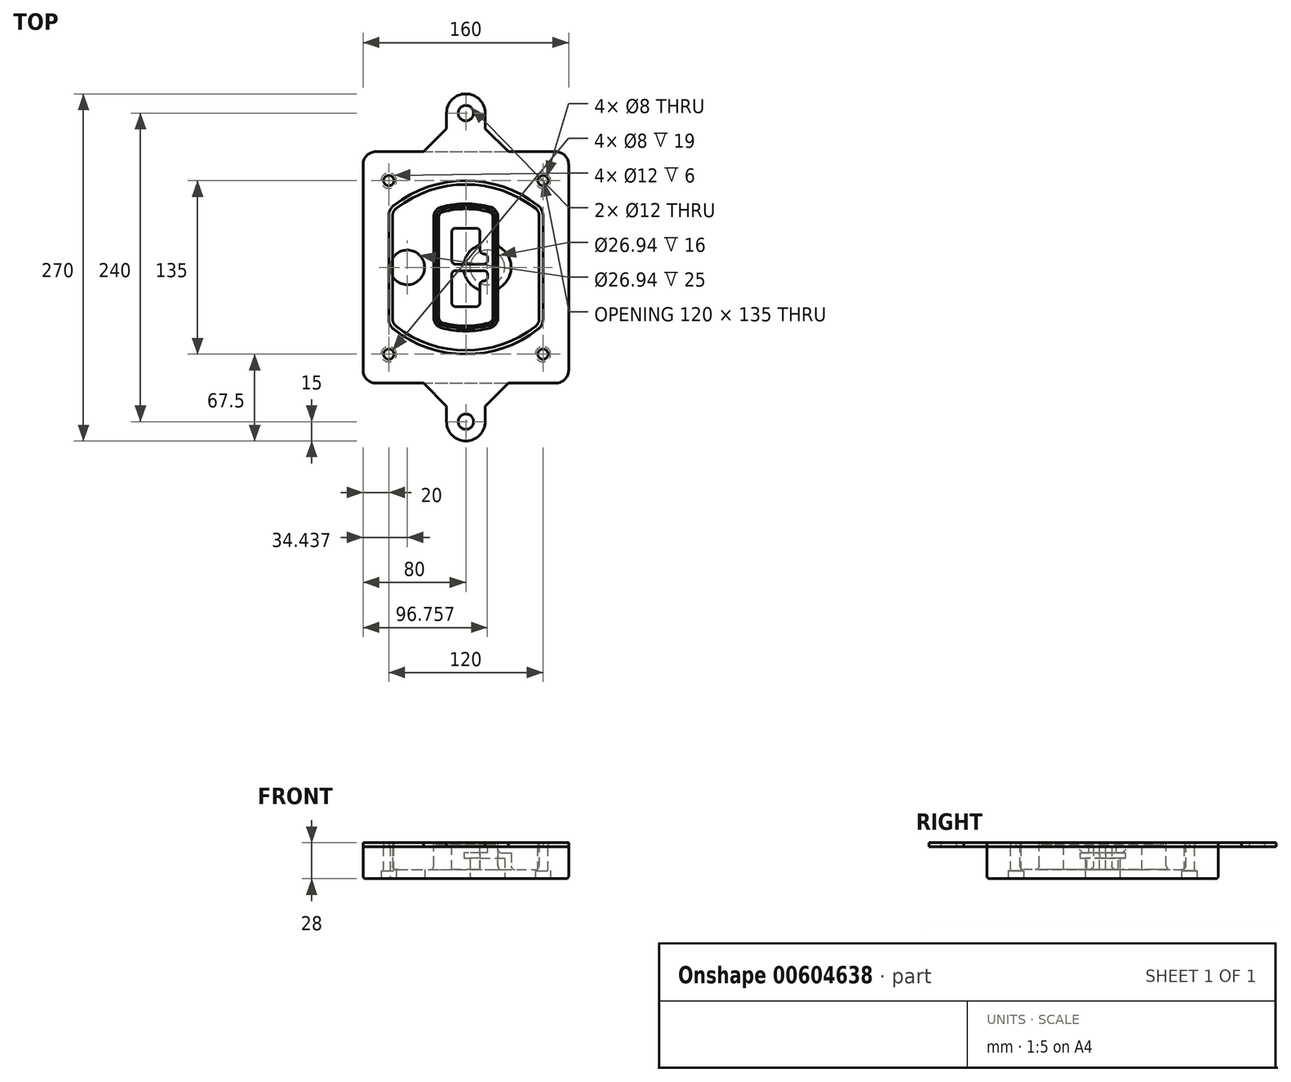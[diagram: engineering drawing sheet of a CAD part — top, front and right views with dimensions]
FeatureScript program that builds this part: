
annotation { "Feature Type Name" : "Feature", "Feature Type Description" : "" }
export const myFeature = defineFeature(function(context is Context, id is Id, definition is map)
    precondition{}
    {
        {
            var Q0;
            Q0=qCreatedBy(makeId("Top.planeOp"),FACE);
            var sketch = newSketch(context, id + "F0", { "sketchPlane" : qUnion([Q0])});
            skPoint(sketch, "E0.rect.middle", {"position": v(0, 0) * mm});
            skLineSegment(sketch, "E1.bottom", {"start": v(-70, -90) * mm, "end": v(70, -90) * mm});
            skLineSegment(sketch, "E1.top", {"start": v(-70, 90) * mm, "end": v(70, 90) * mm});
            skLineSegment(sketch, "E1.left", {"start": v(-80, -80) * mm, "end": v(-80, 80) * mm});
            skLineSegment(sketch, "E1.right", {"start": v(80, -80) * mm, "end": v(80, 80) * mm});
            skLineSegment(sketch, "E2", {"start": v(-80, 90) * mm, "end": v(80, -90) * mm, "construction": true});
            skLineSegment(sketch, "E3", {"start": v(80, 90) * mm, "end": v(-80, -90) * mm, "construction": true});
            skCircle(sketch, "E4", {"center": v(-60, 67.5) * mm, "radius": 4 * mm});
            skCircle(sketch, "E5", {"center": v(60, 67.5) * mm, "radius": 4 * mm});
            skCircle(sketch, "E6", {"center": v(60, -67.5) * mm, "radius": 4 * mm});
            skCircle(sketch, "E7", {"center": v(-60, -67.5) * mm, "radius": 4 * mm});
            skLineSegment(sketch, "E8", {"start": v(-60, 67.5) * mm, "end": v(60, 67.5) * mm, "construction": true});
            skLineSegment(sketch, "E9", {"start": v(60, 67.5) * mm, "end": v(60, -67.5) * mm, "construction": true});
            skLineSegment(sketch, "E10", {"start": v(60, -67.5) * mm, "end": v(-60, -67.5) * mm, "construction": true});
            skLineSegment(sketch, "E11", {"start": v(-60, -67.5) * mm, "end": v(-60, 67.5) * mm, "construction": true});
            skLineSegment(sketch, "E12", {"start": v(-60, 40.3) * mm, "end": v(-60, -40.3) * mm});
            skLineSegment(sketch, "E13", {"start": v(60, 40.3) * mm, "end": v(60, -40.3) * mm});
            skArc(sketch, "E14", {"start": v(56.15, 48.18) * mm, "mid": v(0, 67.5) * mm, "end": v(-56.15, 48.18) * mm});
            skArc(sketch, "E15", {"start": v(-56.15, -48.18) * mm, "mid": v(0, -67.5) * mm, "end": v(56.15, -48.18) * mm});
            skLineSegment(sketch, "E16", {"start": v(-60, 0) * mm, "end": v(60, 0) * mm, "construction": true});
            skPoint(sketch, "E17.visualSharp", {"position": v(-60, -45) * mm});
            skArc(sketch, "E17.filletArc", {"start": v(-60, -40.3) * mm, "mid": v(-58.99, -44.68) * mm, "end": v(-56.15, -48.18) * mm});
            skPoint(sketch, "E18.visualSharp", {"position": v(-60, 45) * mm});
            skArc(sketch, "E18.filletArc", {"start": v(-56.15, 48.18) * mm, "mid": v(-58.99, 44.68) * mm, "end": v(-60, 40.3) * mm});
            skPoint(sketch, "E19.visualSharp", {"position": v(60, 45) * mm});
            skArc(sketch, "E19.filletArc", {"start": v(60, 40.3) * mm, "mid": v(58.99, 44.68) * mm, "end": v(56.15, 48.18) * mm});
            skPoint(sketch, "E20.visualSharp", {"position": v(60, -45) * mm});
            skArc(sketch, "E20.filletArc", {"start": v(56.15, -48.18) * mm, "mid": v(58.99, -44.68) * mm, "end": v(60, -40.3) * mm});
            skPoint(sketch, "E21.visualSharp", {"position": v(-80, 90) * mm});
            skArc(sketch, "E21.filletArc", {"start": v(-70, 90) * mm, "mid": v(-77.07, 87.07) * mm, "end": v(-80, 80) * mm});
            skPoint(sketch, "E22.visualSharp", {"position": v(80, 90) * mm});
            skArc(sketch, "E22.filletArc", {"start": v(80, 80) * mm, "mid": v(77.07, 87.07) * mm, "end": v(70, 90) * mm});
            skPoint(sketch, "E23.visualSharp", {"position": v(80, -90) * mm});
            skArc(sketch, "E23.filletArc", {"start": v(70, -90) * mm, "mid": v(77.07, -87.07) * mm, "end": v(80, -80) * mm});
            skPoint(sketch, "E24.visualSharp", {"position": v(-80, -90) * mm});
            skArc(sketch, "E24.filletArc", {"start": v(-80, -80) * mm, "mid": v(-77.07, -87.07) * mm, "end": v(-70, -90) * mm});
            skArc(sketch, "E25.0", {"start": v(57, 40.3) * mm, "mid": v(56.3, 43.36) * mm, "end": v(54.3, 45.81) * mm});
            skLineSegment(sketch, "E25.1", {"start": v(57, 40.3) * mm, "end": v(57, -40.3) * mm});
            skArc(sketch, "E25.2", {"start": v(54.3, -45.81) * mm, "mid": v(56.3, -43.36) * mm, "end": v(57, -40.3) * mm});
            skArc(sketch, "E25.3", {"start": v(-54.3, -45.81) * mm, "mid": v(0, -64.5) * mm, "end": v(54.3, -45.81) * mm});
            skArc(sketch, "E25.4", {"start": v(-57, -40.3) * mm, "mid": v(-56.3, -43.36) * mm, "end": v(-54.3, -45.81) * mm});
            skArc(sketch, "E25.5", {"start": v(54.3, 45.81) * mm, "mid": v(0, 64.5) * mm, "end": v(-54.3, 45.81) * mm});
            skLineSegment(sketch, "E25.6", {"start": v(-57, 40.3) * mm, "end": v(-57, -40.3) * mm});
            skArc(sketch, "E25.7", {"start": v(-54.3, 45.81) * mm, "mid": v(-56.3, 43.36) * mm, "end": v(-57, 40.3) * mm});
            skArc(sketch, "E26.0", {"start": v(-58.62, 51.33) * mm, "mid": v(-62.58, 46.43) * mm, "end": v(-64, 40.3) * mm});
            skArc(sketch, "E26.1", {"start": v(58.62, 51.33) * mm, "mid": v(0, 71.5) * mm, "end": v(-58.62, 51.33) * mm});
            skArc(sketch, "E26.2", {"start": v(64, 40.3) * mm, "mid": v(62.58, 46.43) * mm, "end": v(58.62, 51.33) * mm});
            skLineSegment(sketch, "E26.3", {"start": v(64, 40.3) * mm, "end": v(64, -40.3) * mm});
            skArc(sketch, "E26.4", {"start": v(58.62, -51.33) * mm, "mid": v(62.58, -46.43) * mm, "end": v(64, -40.3) * mm});
            skLineSegment(sketch, "E26.5", {"start": v(-64, 40.3) * mm, "end": v(-64, -40.3) * mm});
            skArc(sketch, "E26.6", {"start": v(-58.62, -51.33) * mm, "mid": v(0, -71.5) * mm, "end": v(58.62, -51.33) * mm});
            skArc(sketch, "E26.7", {"start": v(-64, -40.3) * mm, "mid": v(-62.58, -46.43) * mm, "end": v(-58.62, -51.33) * mm});
            skSolve(sketch);
        }
        {
            var Q0;
            Q0=makeQuery(id+"F0.imprint","IMPRINT",FACE,{"disambiguationData":[TD([[makeQuery(id+"F0.imprint","IMPRINT",EDGE,{"derivedFrom":sQuery(id+"F0.wireOp",EDGE,"E1.bottom")}),1.0]])]});
            var Q1;
            Q1=makeQuery(id+"F0.imprint","IMPRINT",FACE,{"disambiguationData":[TD([[makeQuery(id+"F0.imprint","IMPRINT",EDGE,{"derivedFrom":sQuery(id+"F0.wireOp",EDGE,"E12")}),1.0]])]});
            var Q2;
            Q2=makeQuery(id+"F0.imprint","IMPRINT",FACE,{"disambiguationData":[TD([[makeQuery(id+"F0.imprint","IMPRINT",EDGE,{"derivedFrom":sQuery(id+"F0.wireOp",EDGE,"E25.0")}),1.0]])]});
            var Q3;
            Q3=makeQuery(id+"F0.imprint","IMPRINT",FACE,{"disambiguationData":[TD([[makeQuery(id+"F0.imprint","IMPRINT",EDGE,{"derivedFrom":sQuery(id+"F0.wireOp",EDGE,"E12")}),-1.0]])]});
            extrude(context, id + "F1", {"entities" : qUnion([Q0, Q1, Q2, Q3]), "oppositeDirection" : true, "depth" : 25 * mm});
        }
        {
            var Q0;
            Q0=makeQuery(id+"F0.imprint","IMPRINT",FACE,{"disambiguationData":[TD([[makeQuery(id+"F0.imprint","IMPRINT",EDGE,{"derivedFrom":sQuery(id+"F0.wireOp",EDGE,"E12")}),1.0]])]});
            extrude(context, id + "F2", {"entities" : qUnion([Q0]), "operationType" : NewBodyOperationType.ADD, "depth" : 3 * mm});
        }
        {
            var Q0;
            Q0=makeQuery(id+"F0.imprint","IMPRINT",FACE,{"disambiguationData":[TD([[makeQuery(id+"F0.imprint","IMPRINT",EDGE,{"derivedFrom":sQuery(id+"F0.wireOp",EDGE,"E25.0")}),1.0]])]});
            extrude(context, id + "F3", {"entities" : qUnion([Q0]), "operationType" : NewBodyOperationType.REMOVE, "oppositeDirection" : true, "depth" : 18 * mm});
        }
        {
            var Q0;
            Q0=makeQuery(id+"F2.opExtrude","CAP_FACE",FACE,{"disambiguationData":[OSD([sQuery(id+"F0.wireOp",EDGE,"E12"),sQuery(id+"F0.wireOp",EDGE,"E13"),sQuery(id+"F0.wireOp",EDGE,"E14"),sQuery(id+"F0.wireOp",EDGE,"E15"),sQuery(id+"F0.wireOp",EDGE,"E17.filletArc"),sQuery(id+"F0.wireOp",EDGE,"E18.filletArc"),sQuery(id+"F0.wireOp",EDGE,"E19.filletArc"),sQuery(id+"F0.wireOp",EDGE,"E20.filletArc"),sQuery(id+"F0.wireOp",EDGE,"E25.0"),sQuery(id+"F0.wireOp",EDGE,"E25.1"),sQuery(id+"F0.wireOp",EDGE,"E25.2"),sQuery(id+"F0.wireOp",EDGE,"E25.3"),sQuery(id+"F0.wireOp",EDGE,"E25.4"),sQuery(id+"F0.wireOp",EDGE,"E25.5"),sQuery(id+"F0.wireOp",EDGE,"E25.6"),sQuery(id+"F0.wireOp",EDGE,"E25.7")])],"isStart":false});
            var sketch = newSketch(context, id + "F4", { "sketchPlane" : qUnion([Q0])});
            skArc(sketch, "E27.0", {"start": v(-19.08, -46.97) * mm, "mid": v(0, -49.5) * mm, "end": v(19.08, -46.97) * mm});
            skArc(sketch, "E28.0", {"start": v(19.08, 46.97) * mm, "mid": v(0, 49.5) * mm, "end": v(-19.08, 46.97) * mm});
            skLineSegment(sketch, "E29", {"start": v(-25, 39.25) * mm, "end": v(-25, -39.25) * mm});
            skLineSegment(sketch, "E30", {"start": v(25, 39.25) * mm, "end": v(25, -39.25) * mm});
            skLineSegment(sketch, "E31", {"start": v(-25, 45.1) * mm, "end": v(25, 45.1) * mm, "construction": true});
            skLineSegment(sketch, "E32", {"start": v(-25, -45.1) * mm, "end": v(25, -45.1) * mm, "construction": true});
            skPoint(sketch, "E33.visualSharp", {"position": v(-25, 45.1) * mm});
            skArc(sketch, "E33.filletArc", {"start": v(-19.08, 46.97) * mm, "mid": v(-23.35, 44.11) * mm, "end": v(-25, 39.25) * mm});
            skPoint(sketch, "E34.visualSharp", {"position": v(25, 45.1) * mm});
            skArc(sketch, "E34.filletArc", {"start": v(25, 39.25) * mm, "mid": v(23.35, 44.11) * mm, "end": v(19.08, 46.97) * mm});
            skPoint(sketch, "E35.visualSharp", {"position": v(25, -45.1) * mm});
            skArc(sketch, "E35.filletArc", {"start": v(19.08, -46.97) * mm, "mid": v(23.35, -44.11) * mm, "end": v(25, -39.25) * mm});
            skPoint(sketch, "E36.visualSharp", {"position": v(-25, -45.1) * mm});
            skArc(sketch, "E36.filletArc", {"start": v(-25, -39.25) * mm, "mid": v(-23.35, -44.11) * mm, "end": v(-19.08, -46.97) * mm});
            skArc(sketch, "E37.0", {"start": v(54.3, 45.81) * mm, "mid": v(0, 64.5) * mm, "end": v(-54.3, 45.81) * mm});
            skArc(sketch, "E37.1", {"start": v(-54.3, 45.81) * mm, "mid": v(-56.3, 43.36) * mm, "end": v(-57, 40.3) * mm});
            skLineSegment(sketch, "E37.2", {"start": v(-57, 40.3) * mm, "end": v(-57, -40.3) * mm});
            skArc(sketch, "E37.3", {"start": v(-57, -40.3) * mm, "mid": v(-56.3, -43.36) * mm, "end": v(-54.3, -45.81) * mm});
            skArc(sketch, "E37.4", {"start": v(-54.3, -45.81) * mm, "mid": v(0, -64.5) * mm, "end": v(54.3, -45.81) * mm});
            skArc(sketch, "E37.5", {"start": v(54.3, -45.81) * mm, "mid": v(56.3, -43.36) * mm, "end": v(57, -40.3) * mm});
            skLineSegment(sketch, "E37.6", {"start": v(57, 40.3) * mm, "end": v(57, -40.3) * mm});
            skArc(sketch, "E37.7", {"start": v(57, 40.3) * mm, "mid": v(56.3, 43.36) * mm, "end": v(54.3, 45.81) * mm});
            skLineSegment(sketch, "E38.0", {"start": v(23, 39.25) * mm, "end": v(23, -39.25) * mm});
            skArc(sketch, "E38.1", {"start": v(18.56, -45.04) * mm, "mid": v(21.76, -42.9) * mm, "end": v(23, -39.25) * mm});
            skArc(sketch, "E38.2", {"start": v(-18.56, -45.04) * mm, "mid": v(0, -47.5) * mm, "end": v(18.56, -45.04) * mm});
            skArc(sketch, "E38.3", {"start": v(-23, -39.25) * mm, "mid": v(-21.76, -42.9) * mm, "end": v(-18.56, -45.04) * mm});
            skLineSegment(sketch, "E38.4", {"start": v(-23, 39.25) * mm, "end": v(-23, -39.25) * mm});
            skArc(sketch, "E38.5", {"start": v(23, 39.25) * mm, "mid": v(21.76, 42.9) * mm, "end": v(18.56, 45.04) * mm});
            skArc(sketch, "E38.6", {"start": v(-18.56, 45.04) * mm, "mid": v(-21.76, 42.9) * mm, "end": v(-23, 39.25) * mm});
            skArc(sketch, "E38.7", {"start": v(18.56, 45.04) * mm, "mid": v(0, 47.5) * mm, "end": v(-18.56, 45.04) * mm});
            skArc(sketch, "E39.0", {"start": v(21, 39.25) * mm, "mid": v(20.18, 41.68) * mm, "end": v(18.04, 43.1) * mm});
            skLineSegment(sketch, "E39.1", {"start": v(21, 39.25) * mm, "end": v(21, -39.25) * mm});
            skArc(sketch, "E39.2", {"start": v(18.04, -43.1) * mm, "mid": v(20.18, -41.68) * mm, "end": v(21, -39.25) * mm});
            skArc(sketch, "E39.3", {"start": v(-18.04, -43.1) * mm, "mid": v(0, -45.5) * mm, "end": v(18.04, -43.1) * mm});
            skArc(sketch, "E39.4", {"start": v(-21, -39.25) * mm, "mid": v(-20.18, -41.68) * mm, "end": v(-18.04, -43.1) * mm});
            skArc(sketch, "E39.5", {"start": v(18.04, 43.1) * mm, "mid": v(0, 45.5) * mm, "end": v(-18.04, 43.1) * mm});
            skLineSegment(sketch, "E39.6", {"start": v(-21, 39.25) * mm, "end": v(-21, -39.25) * mm});
            skArc(sketch, "E39.7", {"start": v(-18.04, 43.1) * mm, "mid": v(-20.18, 41.68) * mm, "end": v(-21, 39.25) * mm});
            skLineSegment(sketch, "E40", {"start": v(-25, 0) * mm, "end": v(25, 0) * mm, "construction": true});
            skLineSegment(sketch, "E41", {"start": v(-11, 5.5) * mm, "end": v(-11, 27.5) * mm});
            skLineSegment(sketch, "E42", {"start": v(-8, 30.5) * mm, "end": v(8, 30.5) * mm});
            skLineSegment(sketch, "E43", {"start": v(11, 27.5) * mm, "end": v(11, 13.5) * mm});
            skLineSegment(sketch, "E44", {"start": v(14, 10.5) * mm, "end": v(14, 10.5) * mm});
            skLineSegment(sketch, "E45", {"start": v(17, 7.5) * mm, "end": v(17, 5.5) * mm});
            skLineSegment(sketch, "E46", {"start": v(14, 2.5) * mm, "end": v(-8, 2.5) * mm});
            skPoint(sketch, "E47.visualSharp", {"position": v(-11, 30.5) * mm});
            skArc(sketch, "E47.filletArc", {"start": v(-8, 30.5) * mm, "mid": v(-10.12, 29.62) * mm, "end": v(-11, 27.5) * mm});
            skPoint(sketch, "E48.visualSharp", {"position": v(11, 30.5) * mm});
            skArc(sketch, "E48.filletArc", {"start": v(11, 27.5) * mm, "mid": v(10.12, 29.62) * mm, "end": v(8, 30.5) * mm});
            skPoint(sketch, "E49.visualSharp", {"position": v(11, 10.5) * mm});
            skArc(sketch, "E49.filletArc", {"start": v(11, 13.5) * mm, "mid": v(11.88, 11.38) * mm, "end": v(14, 10.5) * mm});
            skPoint(sketch, "E50.visualSharp", {"position": v(17, 10.5) * mm});
            skArc(sketch, "E50.filletArc", {"start": v(17, 7.5) * mm, "mid": v(16.12, 9.62) * mm, "end": v(14, 10.5) * mm});
            skPoint(sketch, "E51.visualSharp", {"position": v(17, 2.5) * mm});
            skArc(sketch, "E51.filletArc", {"start": v(14, 2.5) * mm, "mid": v(16.12, 3.38) * mm, "end": v(17, 5.5) * mm});
            skPoint(sketch, "E52.visualSharp", {"position": v(-11, 2.5) * mm});
            skArc(sketch, "E52.filletArc", {"start": v(-11, 5.5) * mm, "mid": v(-10.12, 3.38) * mm, "end": v(-8, 2.5) * mm});
            skLineSegment(sketch, "E53.0.MirrorCS", {"start": v(14, -2.5) * mm, "end": v(-8, -2.5) * mm});
            skArc(sketch, "E54.0.MirrorCS", {"start": v(-11, -5.5) * mm, "mid": v(-10.12, -3.38) * mm, "end": v(-8, -2.5) * mm});
            skLineSegment(sketch, "E55.0.MirrorCS", {"start": v(-11, -5.5) * mm, "end": v(-11, -27.5) * mm});
            skArc(sketch, "E56.0.MirrorCS", {"start": v(-8, -30.5) * mm, "mid": v(-10.12, -29.62) * mm, "end": v(-11, -27.5) * mm});
            skLineSegment(sketch, "E57.0.MirrorCS", {"start": v(-8, -30.5) * mm, "end": v(8, -30.5) * mm});
            skArc(sketch, "E58.0.MirrorCS", {"start": v(11, -27.5) * mm, "mid": v(10.12, -29.62) * mm, "end": v(8, -30.5) * mm});
            skLineSegment(sketch, "E59.0.MirrorCS", {"start": v(11, -27.5) * mm, "end": v(11, -13.5) * mm});
            skArc(sketch, "E60.0.MirrorCS", {"start": v(11, -13.5) * mm, "mid": v(11.88, -11.38) * mm, "end": v(14, -10.5) * mm});
            skArc(sketch, "E61.0.MirrorCS", {"start": v(17, -7.5) * mm, "mid": v(16.12, -9.62) * mm, "end": v(14, -10.5) * mm});
            skLineSegment(sketch, "E62.0.MirrorCS", {"start": v(17, -7.5) * mm, "end": v(17, -5.5) * mm});
            skArc(sketch, "E63.0.MirrorCS", {"start": v(14, -2.5) * mm, "mid": v(16.12, -3.38) * mm, "end": v(17, -5.5) * mm});
            skSolve(sketch);
        }
        {
            var Q0;
            Q0=makeQuery(id+"F4.imprint","IMPRINT",FACE,{"disambiguationData":[TD([[makeQuery(id+"F4.imprint","IMPRINT",EDGE,{"derivedFrom":sQuery(id+"F4.wireOp",EDGE,"E27.0")}),1.0]])]});
            var Q1;
            Q1=makeQuery(id+"F4.imprint","IMPRINT",FACE,{"disambiguationData":[TD([[makeQuery(id+"F4.imprint","IMPRINT",EDGE,{"derivedFrom":sQuery(id+"F4.wireOp",EDGE,"E38.0")}),-1.0]])]});
            var Q2;
            Q2=makeQuery(id+"F4.imprint","IMPRINT",FACE,{"disambiguationData":[TD([[makeQuery(id+"F4.imprint","IMPRINT",EDGE,{"derivedFrom":sQuery(id+"F4.wireOp",EDGE,"E39.0")}),1.0]])]});
            extrude(context, id + "F5", {"entities" : qUnion([Q0, Q1, Q2]), "operationType" : NewBodyOperationType.ADD, "endBound" : BoundingType.UP_TO_NEXT, "oppositeDirection" : true, "depth" : 25 * mm});
        }
        {
            var Q0;
            Q0=makeQuery(id+"F4.imprint","IMPRINT",FACE,{"disambiguationData":[TD([[makeQuery(id+"F4.imprint","IMPRINT",EDGE,{"derivedFrom":sQuery(id+"F4.wireOp",EDGE,"E38.0")}),-1.0]])]});
            extrude(context, id + "F6", {"entities" : qUnion([Q0]), "operationType" : NewBodyOperationType.REMOVE, "oppositeDirection" : true, "depth" : 2 * mm});
        }
        {
            var Q0;
            Q0=makeQuery(id+"F1.opExtrude","CAP_FACE",FACE,{"disambiguationData":[OSD([sQuery(id+"F0.wireOp",EDGE,"E1.bottom"),sQuery(id+"F0.wireOp",EDGE,"E1.top"),sQuery(id+"F0.wireOp",EDGE,"E1.left"),sQuery(id+"F0.wireOp",EDGE,"E1.right"),sQuery(id+"F0.wireOp",EDGE,"E4"),sQuery(id+"F0.wireOp",EDGE,"E5"),sQuery(id+"F0.wireOp",EDGE,"E6"),sQuery(id+"F0.wireOp",EDGE,"E7"),sQuery(id+"F0.wireOp",EDGE,"E21.filletArc"),sQuery(id+"F0.wireOp",EDGE,"E22.filletArc"),sQuery(id+"F0.wireOp",EDGE,"E23.filletArc"),sQuery(id+"F0.wireOp",EDGE,"E24.filletArc")])],"isStart":false});
            var sketch = newSketch(context, id + "F7", { "sketchPlane" : qUnion([Q0])});
            skCircle(sketch, "E64", {"center": v(16.76, 0) * mm, "radius": 13.47 * mm});
            skCircle(sketch, "E65", {"center": v(-45.56, 0) * mm, "radius": 13.47 * mm});
            skLineSegment(sketch, "E66", {"start": v(80, 0) * mm, "end": v(-80, 0) * mm});
            skCircle(sketch, "E67", {"center": v(16.76, 0) * mm, "radius": 18.47 * mm});
            skCircle(sketch, "E68", {"center": v(60, -67.5) * mm, "radius": 6 * mm});
            skCircle(sketch, "E69", {"center": v(-60, -67.5) * mm, "radius": 6 * mm});
            skCircle(sketch, "E70", {"center": v(-60, 67.5) * mm, "radius": 6 * mm});
            skCircle(sketch, "E71", {"center": v(60, 67.5) * mm, "radius": 6 * mm});
            skSolve(sketch);
        }
        {
            var Q0;
            {var subQ1=sQuery(id+"F7.wireOp",EDGE,"E66");var subQ4=sQuery(id+"F7.wireOp",EDGE,"E64");var subQ6=makeQuery(id+"F7.imprint","INTERSECT",VERTEX,{"disambiguationData":[OD(0.0)],"derivedFrom":[subQ4,subQ1]});Q0=makeQuery(id+"F7.imprint","IMPRINT",FACE,{"disambiguationData":[TD([[makeQuery(id+"F7.imprint","IMPRINT",EDGE,{"disambiguationData":[TD([[subQ6,-1.0]])],"derivedFrom":subQ4}),-1.0]])]});}
            var Q1;
            {var subQ0=sQuery(id+"F7.wireOp",EDGE,"E66");var subQ1=sQuery(id+"F7.wireOp",EDGE,"E64");var subQ3=makeQuery(id+"F7.imprint","INTERSECT",VERTEX,{"disambiguationData":[OD(0.0)],"derivedFrom":[subQ1,subQ0]});Q1=makeQuery(id+"F7.imprint","IMPRINT",FACE,{"disambiguationData":[TD([[makeQuery(id+"F7.imprint","IMPRINT",EDGE,{"disambiguationData":[TD([[subQ3,-1.0]])],"derivedFrom":subQ1}),1.0]])]});}
            var Q2;
            {var subQ0=sQuery(id+"F7.wireOp",EDGE,"E66");var subQ1=sQuery(id+"F7.wireOp",EDGE,"E64");var subQ3=makeQuery(id+"F7.imprint","INTERSECT",VERTEX,{"disambiguationData":[OD(0.0)],"derivedFrom":[subQ1,subQ0]});Q2=makeQuery(id+"F7.imprint","IMPRINT",FACE,{"disambiguationData":[TD([[makeQuery(id+"F7.imprint","IMPRINT",EDGE,{"disambiguationData":[TD([[subQ3,1.0]])],"derivedFrom":subQ1}),1.0]])]});}
            var Q3;
            {var subQ1=sQuery(id+"F7.wireOp",EDGE,"E66");var subQ4=sQuery(id+"F7.wireOp",EDGE,"E64");var subQ6=makeQuery(id+"F7.imprint","INTERSECT",VERTEX,{"disambiguationData":[OD(0.0)],"derivedFrom":[subQ4,subQ1]});Q3=makeQuery(id+"F7.imprint","IMPRINT",FACE,{"disambiguationData":[TD([[makeQuery(id+"F7.imprint","IMPRINT",EDGE,{"disambiguationData":[TD([[subQ6,1.0]])],"derivedFrom":subQ4}),-1.0]])]});}
            extrude(context, id + "F8", {"entities" : qUnion([Q0, Q1, Q2, Q3]), "operationType" : NewBodyOperationType.ADD, "oppositeDirection" : true, "depth" : 20 * mm});
        }
        {
            var Q0;
            {var subQ0=sQuery(id+"F7.wireOp",EDGE,"E66");var subQ1=sQuery(id+"F7.wireOp",EDGE,"E64");var subQ3=makeQuery(id+"F7.imprint","INTERSECT",VERTEX,{"disambiguationData":[OD(0.0)],"derivedFrom":[subQ1,subQ0]});Q0=makeQuery(id+"F7.imprint","IMPRINT",FACE,{"disambiguationData":[TD([[makeQuery(id+"F7.imprint","IMPRINT",EDGE,{"disambiguationData":[TD([[subQ3,-1.0]])],"derivedFrom":subQ1}),1.0]])]});}
            var Q1;
            {var subQ0=sQuery(id+"F7.wireOp",EDGE,"E66");var subQ1=sQuery(id+"F7.wireOp",EDGE,"E64");var subQ3=makeQuery(id+"F7.imprint","INTERSECT",VERTEX,{"disambiguationData":[OD(0.0)],"derivedFrom":[subQ1,subQ0]});Q1=makeQuery(id+"F7.imprint","IMPRINT",FACE,{"disambiguationData":[TD([[makeQuery(id+"F7.imprint","IMPRINT",EDGE,{"disambiguationData":[TD([[subQ3,1.0]])],"derivedFrom":subQ1}),1.0]])]});}
            extrude(context, id + "F9", {"entities" : qUnion([Q0, Q1]), "operationType" : NewBodyOperationType.REMOVE, "oppositeDirection" : true, "depth" : 16 * mm});
        }
        {
            var Q0;
            {var subQ0=sQuery(id+"F7.wireOp",EDGE,"E66");var subQ1=sQuery(id+"F7.wireOp",EDGE,"E65");var subQ3=makeQuery(id+"F7.imprint","INTERSECT",VERTEX,{"disambiguationData":[OD(0.0)],"derivedFrom":[subQ1,subQ0]});Q0=makeQuery(id+"F7.imprint","IMPRINT",FACE,{"disambiguationData":[TD([[makeQuery(id+"F7.imprint","IMPRINT",EDGE,{"disambiguationData":[TD([[subQ3,-1.0]])],"derivedFrom":subQ1}),1.0]])]});}
            var Q1;
            {var subQ0=sQuery(id+"F7.wireOp",EDGE,"E66");var subQ1=sQuery(id+"F7.wireOp",EDGE,"E65");var subQ3=makeQuery(id+"F7.imprint","INTERSECT",VERTEX,{"disambiguationData":[OD(0.0)],"derivedFrom":[subQ1,subQ0]});Q1=makeQuery(id+"F7.imprint","IMPRINT",FACE,{"disambiguationData":[TD([[makeQuery(id+"F7.imprint","IMPRINT",EDGE,{"disambiguationData":[TD([[subQ3,1.0]])],"derivedFrom":subQ1}),1.0]])]});}
            extrude(context, id + "F10", {"entities" : qUnion([Q0, Q1]), "operationType" : NewBodyOperationType.REMOVE, "oppositeDirection" : true, "depth" : 25 * mm});
        }
        {
            var Q0;
            Q0=makeQuery(id+"F7.imprint","IMPRINT",FACE,{"disambiguationData":[TD([[makeQuery(id+"F7.imprint","IMPRINT",EDGE,{"derivedFrom":sQuery(id+"F7.wireOp",EDGE,"E68")}),1.0]])]});
            var Q1;
            Q1=makeQuery(id+"F7.imprint","IMPRINT",FACE,{"disambiguationData":[TD([[makeQuery(id+"F7.imprint","IMPRINT",EDGE,{"derivedFrom":makeQuery(id+"F1.opExtrude","CAP_EDGE",EDGE,{"disambiguationData":[OSD([sQuery(id+"F0.wireOp",EDGE,"E5")])],"isStart":false})}),-1.0]])]});
            var Q2;
            Q2=makeQuery(id+"F7.imprint","IMPRINT",FACE,{"disambiguationData":[TD([[makeQuery(id+"F7.imprint","IMPRINT",EDGE,{"derivedFrom":sQuery(id+"F7.wireOp",EDGE,"E69")}),1.0]])]});
            var Q3;
            Q3=makeQuery(id+"F7.imprint","IMPRINT",FACE,{"disambiguationData":[TD([[makeQuery(id+"F7.imprint","IMPRINT",EDGE,{"derivedFrom":makeQuery(id+"F1.opExtrude","CAP_EDGE",EDGE,{"disambiguationData":[OSD([sQuery(id+"F0.wireOp",EDGE,"E4")])],"isStart":false})}),-1.0]])]});
            var Q4;
            Q4=makeQuery(id+"F7.imprint","IMPRINT",FACE,{"disambiguationData":[TD([[makeQuery(id+"F7.imprint","IMPRINT",EDGE,{"derivedFrom":sQuery(id+"F7.wireOp",EDGE,"E70")}),1.0]])]});
            var Q5;
            Q5=makeQuery(id+"F7.imprint","IMPRINT",FACE,{"disambiguationData":[TD([[makeQuery(id+"F7.imprint","IMPRINT",EDGE,{"derivedFrom":makeQuery(id+"F1.opExtrude","CAP_EDGE",EDGE,{"disambiguationData":[OSD([sQuery(id+"F0.wireOp",EDGE,"E7")])],"isStart":false})}),-1.0]])]});
            var Q6;
            Q6=makeQuery(id+"F7.imprint","IMPRINT",FACE,{"disambiguationData":[TD([[makeQuery(id+"F7.imprint","IMPRINT",EDGE,{"derivedFrom":sQuery(id+"F7.wireOp",EDGE,"E71")}),1.0]])]});
            var Q7;
            Q7=makeQuery(id+"F7.imprint","IMPRINT",FACE,{"disambiguationData":[TD([[makeQuery(id+"F7.imprint","IMPRINT",EDGE,{"derivedFrom":makeQuery(id+"F1.opExtrude","CAP_EDGE",EDGE,{"disambiguationData":[OSD([sQuery(id+"F0.wireOp",EDGE,"E6")])],"isStart":false})}),-1.0]])]});
            extrude(context, id + "F11", {"entities" : qUnion([Q0, Q1, Q2, Q3, Q4, Q5, Q6, Q7]), "operationType" : NewBodyOperationType.REMOVE, "oppositeDirection" : true, "depth" : 6 * mm});
        }
        {
            var Q0;
            Q0=makeQuery(id+"F9.boolean.opBoolean","COPY",FACE,{"derivedFrom":makeQuery(id+"F9.opExtrude","CAP_FACE",FACE,{"disambiguationData":[OSD([sQuery(id+"F7.wireOp",EDGE,"E64")])],"isStart":false})});
            var sketch = newSketch(context, id + "F12", { "sketchPlane" : qUnion([Q0])});
            skArc(sketch, "E72.0", {"start": v(11, 17.55) * mm, "mid": v(2.57, 11.82) * mm, "end": v(-1.54, 2.5) * mm});
            skArc(sketch, "E72.1", {"start": v(-1.54, -2.5) * mm, "mid": v(2.57, -11.82) * mm, "end": v(11, -17.55) * mm});
            skLineSegment(sketch, "E73", {"start": v(-1.54, -2.5) * mm, "end": v(14, -2.5) * mm});
            skLineSegment(sketch, "E74.0", {"start": v(14, 2.5) * mm, "end": v(-1.54, 2.5) * mm});
            skArc(sketch, "E74.1", {"start": v(14, 2.5) * mm, "mid": v(16.12, 3.38) * mm, "end": v(17, 5.5) * mm});
            skLineSegment(sketch, "E74.2", {"start": v(17, 7.5) * mm, "end": v(17, 5.5) * mm});
            skArc(sketch, "E74.3", {"start": v(17, 7.5) * mm, "mid": v(16.12, 9.62) * mm, "end": v(14, 10.5) * mm});
            skArc(sketch, "E74.4", {"start": v(11, 13.5) * mm, "mid": v(11.88, 11.38) * mm, "end": v(14, 10.5) * mm});
            skLineSegment(sketch, "E74.5", {"start": v(11, 17.55) * mm, "end": v(11, 13.5) * mm});
            skLineSegment(sketch, "E74.7", {"start": v(14, -2.5) * mm, "end": v(-1.54, -2.5) * mm});
            skArc(sketch, "E74.8", {"start": v(14, -2.5) * mm, "mid": v(16.12, -3.38) * mm, "end": v(17, -5.5) * mm});
            skLineSegment(sketch, "E74.9", {"start": v(17, -7.5) * mm, "end": v(17, -5.5) * mm});
            skArc(sketch, "E74.10", {"start": v(17, -7.5) * mm, "mid": v(16.12, -9.62) * mm, "end": v(14, -10.5) * mm});
            skArc(sketch, "E74.11", {"start": v(11, -13.5) * mm, "mid": v(11.88, -11.38) * mm, "end": v(14, -10.5) * mm});
            skLineSegment(sketch, "E74.12", {"start": v(11, -17.55) * mm, "end": v(11, -13.5) * mm});
            skPoint(sketch, "E75.orphan", {"position": v(11, -27.5) * mm});
            skPoint(sketch, "E76.orphan", {"position": v(-8, -2.5) * mm});
            skPoint(sketch, "E77.orphan", {"position": v(-8, 2.5) * mm});
            skPoint(sketch, "E78.orphan", {"position": v(11, 27.5) * mm});
            skSolve(sketch);
        }
        {
            var Q0;
            {var subQ7=sQuery(id+"F12.wireOp",EDGE,"E72.0");var subQ14=sQuery(id+"F12.wireOp",EDGE,"E72.1");var subQ16=sQuery(id+"F12.wireOp",EDGE,"E74.1");var subQ18=sQuery(id+"F12.wireOp",EDGE,"E74.8");Q0=qUnion([makeQuery(id+"F12.imprint","IMPRINT",FACE,{"disambiguationData":[TD([[makeQuery(id+"F12.imprint","IMPRINT",EDGE,{"derivedFrom":subQ7}),1.0]])]}),makeQuery(id+"F12.imprint","IMPRINT",FACE,{"disambiguationData":[TD([[makeQuery(id+"F12.imprint","IMPRINT",EDGE,{"derivedFrom":subQ14}),1.0]])]}),makeQuery(id+"F12.imprint","IMPRINT",FACE,{"disambiguationData":[TD([[makeQuery(id+"F12.imprint","IMPRINT",EDGE,{"derivedFrom":subQ16}),1.0]])]}),makeQuery(id+"F12.imprint","IMPRINT",FACE,{"disambiguationData":[TD([[makeQuery(id+"F12.imprint","IMPRINT",EDGE,{"derivedFrom":subQ18}),-1.0]])]})]);}
            var Q1;
            Q1=makeQuery(id+"F5.boolean.opBoolean","SPLIT",FACE,{"disambiguationData":[TD([makeQuery(id+"F5.opExtrude","SWEPT_FACE",FACE,{"disambiguationData":[OSD([sQuery(id+"F4.wireOp",EDGE,"E41")])]})])],"derivedFrom":makeQuery(id+"F3.boolean.opBoolean","COPY",FACE,{"derivedFrom":makeQuery(id+"F3.opExtrude","CAP_FACE",FACE,{"disambiguationData":[OSD([sQuery(id+"F0.wireOp",EDGE,"E25.0"),sQuery(id+"F0.wireOp",EDGE,"E25.1"),sQuery(id+"F0.wireOp",EDGE,"E25.2"),sQuery(id+"F0.wireOp",EDGE,"E25.3"),sQuery(id+"F0.wireOp",EDGE,"E25.4"),sQuery(id+"F0.wireOp",EDGE,"E25.5"),sQuery(id+"F0.wireOp",EDGE,"E25.6"),sQuery(id+"F0.wireOp",EDGE,"E25.7")])],"isStart":false})})});
            extrude(context, id + "F13", {"entities" : qUnion([Q0]), "operationType" : NewBodyOperationType.REMOVE, "endBound" : BoundingType.UP_TO_SURFACE, "endBoundEntityFace" : qUnion([Q1]), "depth" : 25 * mm});
        }
        {
            var Q0;
            Q0=makeQuery(id+"F3.boolean.opBoolean","COPY",EDGE,{"derivedFrom":makeQuery(id+"F3.opExtrude","CAP_EDGE",EDGE,{"disambiguationData":[OSD([sQuery(id+"F0.wireOp",EDGE,"E25.6")])],"isStart":false})});
            var Q1;
            Q1=makeQuery(id+"F8.boolean.opBoolean","INTERSECT",EDGE,{"derivedFrom":[makeQuery(id+"F5.opExtrude","SWEPT_FACE",FACE,{"disambiguationData":[OSD([sQuery(id+"F4.wireOp",EDGE,"E30")])]}),makeQuery(id+"F8.opExtrude","CAP_FACE",FACE,{"disambiguationData":[OSD([sQuery(id+"F7.wireOp",EDGE,"E67")])],"isStart":false})]});
            var Q2;
            Q2=makeQuery(id+"F8.boolean.opBoolean","INTERSECT",EDGE,{"disambiguationData":[OD(1.0)],"derivedFrom":[makeQuery(id+"F5.opExtrude","SWEPT_FACE",FACE,{"disambiguationData":[OSD([sQuery(id+"F4.wireOp",EDGE,"E30")])]}),makeQuery(id+"F8.opExtrude","SWEPT_FACE",FACE,{"disambiguationData":[OSD([sQuery(id+"F7.wireOp",EDGE,"E67")])]})]});
            var Q3;
            {var subQ0=sQuery(id+"F4.wireOp",EDGE,"E30");Q3=makeQuery(id+"F8.boolean.opBoolean","SPLIT",EDGE,{"disambiguationData":[TD([makeQuery(id+"F5.opExtrude","SWEPT_FACE",FACE,{"disambiguationData":[OSD([sQuery(id+"F4.wireOp",EDGE,"E35.filletArc")])]})])],"derivedFrom":makeQuery(id+"F5.opExtrude","CAP_EDGE",EDGE,{"disambiguationData":[OSD([subQ0])],"isStart":false})});}
            var Q4;
            {var subQ0=sQuery(id+"F0.wireOp",EDGE,"E25.7");var subQ1=sQuery(id+"F0.wireOp",EDGE,"E25.1");var subQ2=sQuery(id+"F0.wireOp",EDGE,"E25.6");var subQ3=sQuery(id+"F0.wireOp",EDGE,"E25.5");var subQ4=sQuery(id+"F0.wireOp",EDGE,"E25.4");var subQ5=sQuery(id+"F0.wireOp",EDGE,"E25.0");var subQ6=sQuery(id+"F0.wireOp",EDGE,"E25.2");var subQ7=sQuery(id+"F0.wireOp",EDGE,"E25.3");Q4=makeQuery(id+"F8.boolean.opBoolean","INTERSECT",EDGE,{"derivedFrom":[makeQuery(id+"F5.boolean.opBoolean","SPLIT",FACE,{"disambiguationData":[TD([makeQuery(id+"F2.opExtrude","SWEPT_FACE",FACE,{"disambiguationData":[OSD([subQ5])]})])],"derivedFrom":makeQuery(id+"F3.boolean.opBoolean","COPY",FACE,{"derivedFrom":makeQuery(id+"F3.opExtrude","CAP_FACE",FACE,{"disambiguationData":[OSD([subQ5,subQ1,subQ6,subQ7,subQ4,subQ3,subQ2,subQ0])],"isStart":false})})}),makeQuery(id+"F8.opExtrude","SWEPT_FACE",FACE,{"disambiguationData":[OSD([sQuery(id+"F7.wireOp",EDGE,"E67")])]})]});}
            var Q5;
            Q5=makeQuery(id+"F8.boolean.opBoolean","INTERSECT",EDGE,{"disambiguationData":[OD(0.0)],"derivedFrom":[makeQuery(id+"F5.opExtrude","SWEPT_FACE",FACE,{"disambiguationData":[OSD([sQuery(id+"F4.wireOp",EDGE,"E30")])]}),makeQuery(id+"F8.opExtrude","SWEPT_FACE",FACE,{"disambiguationData":[OSD([sQuery(id+"F7.wireOp",EDGE,"E67")])]})]});
            fillet(context, id + "F14", {"entities" : qUnion([Q0, Q1, Q2, Q3, Q4, Q5]), "radius" : 3 * mm, "tangentPropagation" : true, "allowEdgeOverflow" : false});
        }
        {
            var Q0;
            Q0=makeQuery(id+"F1.opExtrude","CAP_EDGE",EDGE,{"disambiguationData":[OSD([sQuery(id+"F0.wireOp",EDGE,"E1.bottom")])],"isStart":false});
            fillet(context, id + "F15", {"entities" : qUnion([Q0]), "radius" : 2 * mm, "tangentPropagation" : true, "allowEdgeOverflow" : false});
        }
        {
            var Q0;
            {var subQ0=sQuery(id+"F0.wireOp",EDGE,"E21.filletArc");var subQ1=sQuery(id+"F0.wireOp",EDGE,"E7");var subQ2=sQuery(id+"F0.wireOp",EDGE,"E6");var subQ3=sQuery(id+"F0.wireOp",EDGE,"E5");var subQ4=sQuery(id+"F0.wireOp",EDGE,"E4");var subQ5=sQuery(id+"F0.wireOp",EDGE,"E22.filletArc");var subQ6=sQuery(id+"F0.wireOp",EDGE,"E1.bottom");var subQ7=sQuery(id+"F0.wireOp",EDGE,"E1.right");var subQ8=sQuery(id+"F0.wireOp",EDGE,"E1.top");var subQ9=sQuery(id+"F0.wireOp",EDGE,"E1.left");var subQ10=sQuery(id+"F0.wireOp",EDGE,"E23.filletArc");var subQ11=sQuery(id+"F0.wireOp",EDGE,"E24.filletArc");Q0=makeQuery(id+"F2.boolean.opBoolean","SPLIT",FACE,{"disambiguationData":[TD([makeQuery(id+"F1.opExtrude","SWEPT_FACE",FACE,{"disambiguationData":[OSD([subQ6])]})])],"derivedFrom":makeQuery(id+"F1.opExtrude","CAP_FACE",FACE,{"disambiguationData":[OSD([subQ6,subQ8,subQ9,subQ7,subQ4,subQ3,subQ2,subQ1,subQ0,subQ5,subQ10,subQ11])],"isStart":true})});}
            var sketch = newSketch(context, id + "F16", { "sketchPlane" : qUnion([Q0])});
            skLineSegment(sketch, "E79", {"start": v(-33, 90) * mm, "end": v(-15, 108) * mm});
            skLineSegment(sketch, "E80", {"start": v(-15, 108) * mm, "end": v(-15, 120) * mm});
            skLineSegment(sketch, "E81", {"start": v(33, 90) * mm, "end": v(15, 108) * mm});
            skLineSegment(sketch, "E82", {"start": v(15, 108) * mm, "end": v(15, 120) * mm});
            skCircle(sketch, "E83", {"center": v(0, 120) * mm, "radius": 6 * mm});
            skArc(sketch, "E84", {"start": v(-15, 120) * mm, "mid": v(0, 135) * mm, "end": v(15, 120) * mm});
            skLineSegment(sketch, "E85", {"start": v(0, 120) * mm, "end": v(0, 90) * mm, "construction": true});
            skLineSegment(sketch, "E86", {"start": v(-80, 0) * mm, "end": v(80, 0) * mm, "construction": true});
            skPoint(sketch, "E86.startSnap0", {"position": v(-80, 0) * mm});
            skLineSegment(sketch, "E87.MirrorCS", {"start": v(-15, -108) * mm, "end": v(-15, -120) * mm});
            skLineSegment(sketch, "E88.MirrorCS", {"start": v(15, -108) * mm, "end": v(15, -120) * mm});
            skLineSegment(sketch, "E89.MirrorCS", {"start": v(-33, -90) * mm, "end": v(-15, -108) * mm});
            skLineSegment(sketch, "E90.MirrorCS", {"start": v(33, -90) * mm, "end": v(15, -108) * mm});
            skCircle(sketch, "E91.MirrorC", {"center": v(0, -120) * mm, "radius": 6 * mm});
            skArc(sketch, "E92.MirrorCS", {"start": v(-15, -120) * mm, "mid": v(0, -135) * mm, "end": v(15, -120) * mm});
            skLineSegment(sketch, "E93.MirrorCS", {"start": v(0, -120) * mm, "end": v(0, -90) * mm, "construction": true});
            skLineSegment(sketch, "E94.0.0", {"start": v(70, 90) * mm, "end": v(-70, 90) * mm});
            skArc(sketch, "E94.0.1", {"start": v(-70, 90) * mm, "mid": v(-77.07, 87.07) * mm, "end": v(-80, 80) * mm});
            skLineSegment(sketch, "E94.0.2", {"start": v(-80, 80) * mm, "end": v(-80, -80) * mm});
            skArc(sketch, "E94.0.3", {"start": v(-80, -80) * mm, "mid": v(-77.07, -87.07) * mm, "end": v(-70, -90) * mm});
            skLineSegment(sketch, "E94.0.4", {"start": v(-70, -90) * mm, "end": v(70, -90) * mm});
            skArc(sketch, "E94.0.5", {"start": v(70, -90) * mm, "mid": v(77.07, -87.07) * mm, "end": v(80, -80) * mm});
            skLineSegment(sketch, "E94.0.6", {"start": v(80, -80) * mm, "end": v(80, 80) * mm});
            skArc(sketch, "E94.0.7", {"start": v(80, 80) * mm, "mid": v(77.07, 87.07) * mm, "end": v(70, 90) * mm});
            skLineSegment(sketch, "E95.0", {"start": v(60, 40.3) * mm, "end": v(60, -40.3) * mm});
            skArc(sketch, "E96.0", {"start": v(56.15, -48.18) * mm, "mid": v(58.99, -44.68) * mm, "end": v(60, -40.3) * mm});
            skArc(sketch, "E97.0", {"start": v(-56.15, -48.18) * mm, "mid": v(0, -67.5) * mm, "end": v(56.15, -48.18) * mm});
            skLineSegment(sketch, "E98.0", {"start": v(-60, 40.3) * mm, "end": v(-60, -40.3) * mm});
            skArc(sketch, "E99.0", {"start": v(-60, -40.3) * mm, "mid": v(-58.99, -44.68) * mm, "end": v(-56.15, -48.18) * mm});
            skArc(sketch, "E100.0", {"start": v(-56.15, 48.18) * mm, "mid": v(-58.99, 44.68) * mm, "end": v(-60, 40.3) * mm});
            skArc(sketch, "E101.0", {"start": v(56.15, 48.18) * mm, "mid": v(0, 67.5) * mm, "end": v(-56.15, 48.18) * mm});
            skArc(sketch, "E102.0", {"start": v(60, 40.3) * mm, "mid": v(58.99, 44.68) * mm, "end": v(56.15, 48.18) * mm});
            skCircle(sketch, "E103.0", {"center": v(-60, -67.5) * mm, "radius": 4 * mm});
            skCircle(sketch, "E104.0", {"center": v(-60, 67.5) * mm, "radius": 4 * mm});
            skCircle(sketch, "E105.0", {"center": v(60, 67.5) * mm, "radius": 4 * mm});
            skCircle(sketch, "E106.0", {"center": v(60, -67.5) * mm, "radius": 4 * mm});
            skSolve(sketch);
        }
        {
            var Q0;
            Q0 = qSketchRegion(id + "F16", true);
            var Q1;
            Q1=makeQuery(id+"F2.opExtrude","CAP_FACE",FACE,{"disambiguationData":[OSD([sQuery(id+"F0.wireOp",EDGE,"E12"),sQuery(id+"F0.wireOp",EDGE,"E13"),sQuery(id+"F0.wireOp",EDGE,"E14"),sQuery(id+"F0.wireOp",EDGE,"E15"),sQuery(id+"F0.wireOp",EDGE,"E17.filletArc"),sQuery(id+"F0.wireOp",EDGE,"E18.filletArc"),sQuery(id+"F0.wireOp",EDGE,"E19.filletArc"),sQuery(id+"F0.wireOp",EDGE,"E20.filletArc"),sQuery(id+"F0.wireOp",EDGE,"E25.0"),sQuery(id+"F0.wireOp",EDGE,"E25.1"),sQuery(id+"F0.wireOp",EDGE,"E25.2"),sQuery(id+"F0.wireOp",EDGE,"E25.3"),sQuery(id+"F0.wireOp",EDGE,"E25.4"),sQuery(id+"F0.wireOp",EDGE,"E25.5"),sQuery(id+"F0.wireOp",EDGE,"E25.6"),sQuery(id+"F0.wireOp",EDGE,"E25.7")])],"isStart":false});
            extrude(context, id + "F17", {"entities" : qUnion([Q0]), "endBound" : BoundingType.UP_TO_SURFACE, "depth" : 25 * mm, "endBoundEntityFace" : qUnion([Q1]), "offsetDistance" : 25 * mm});
        }
    });
